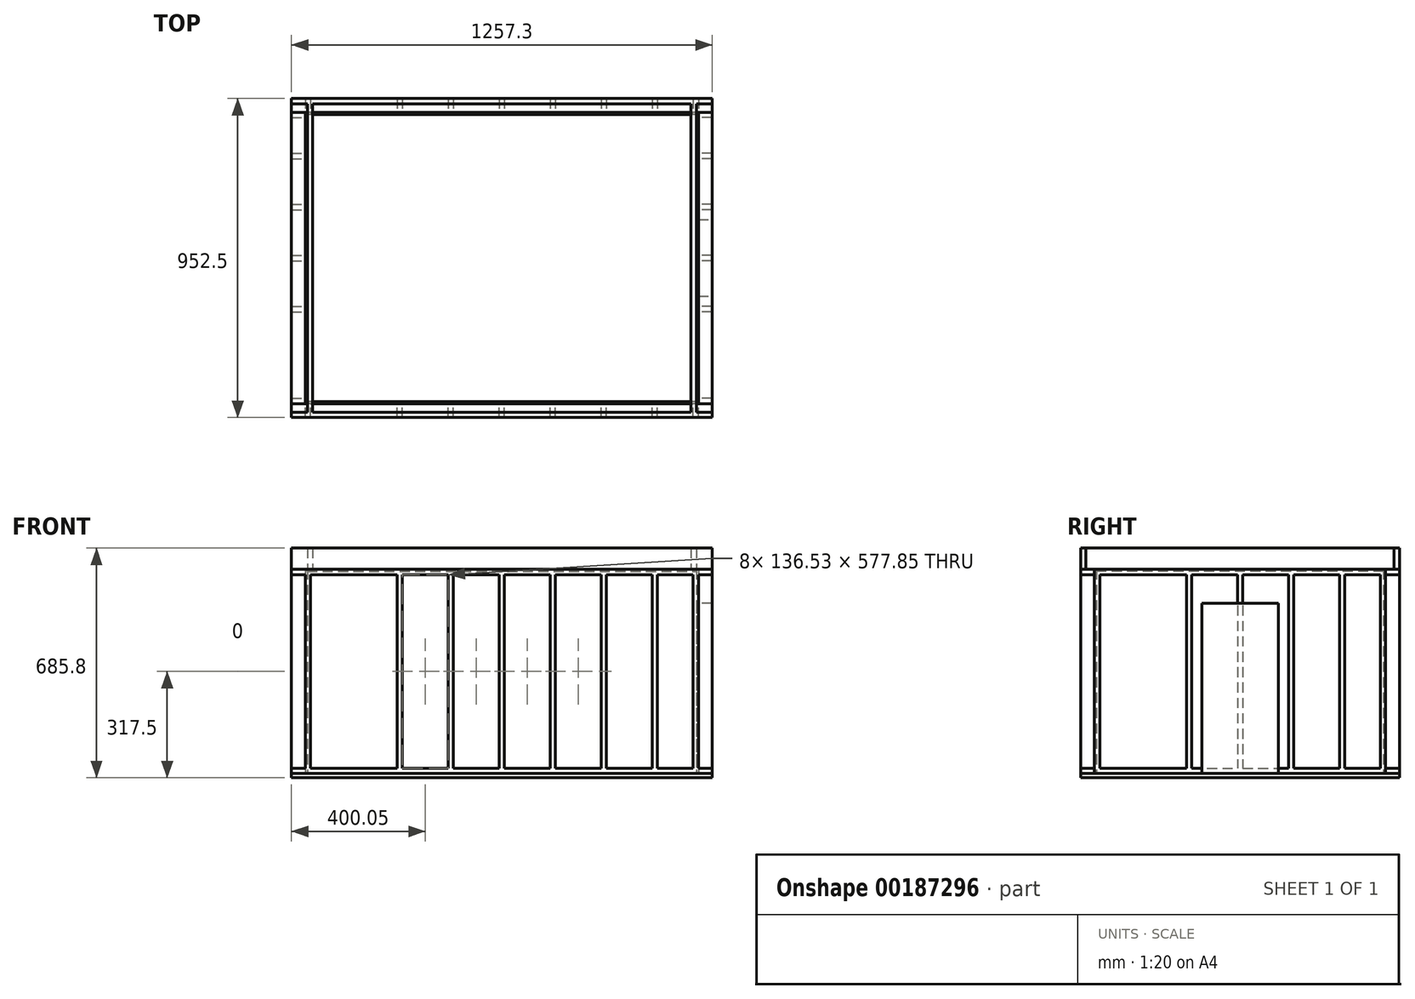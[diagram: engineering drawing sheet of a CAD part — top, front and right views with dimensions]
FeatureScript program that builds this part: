
annotation { "Feature Type Name" : "Feature", "Feature Type Description" : "" }
export const myFeature = defineFeature(function(context is Context, id is Id, definition is map)
    precondition{}
    {
        {
            var Q0;
            Q0=qCreatedBy(makeId("Top.planeOp"),FACE);
            var sketch = newSketch(context, id + "F0", { "sketchPlane" : qUnion([Q0])});
            skLineSegment(sketch, "E0.bottom", {"start": v(587.38, 434.98) * mm, "end": v(-587.38, 434.98) * mm});
            skLineSegment(sketch, "E0.top", {"start": v(587.38, -434.98) * mm, "end": v(-587.38, -434.98) * mm});
            skLineSegment(sketch, "E0.left", {"start": v(587.38, 434.98) * mm, "end": v(587.38, -434.98) * mm});
            skLineSegment(sketch, "E0.right", {"start": v(-587.38, 434.98) * mm, "end": v(-587.38, -434.98) * mm});
            skPoint(sketch, "E0.middle", {"position": v(0, 0) * mm});
            skLineSegment(sketch, "E1.0", {"start": v(581.02, 428.63) * mm, "end": v(-581.03, 428.63) * mm});
            skLineSegment(sketch, "E1.1", {"start": v(581.02, 428.63) * mm, "end": v(581.02, -428.63) * mm});
            skLineSegment(sketch, "E1.2", {"start": v(581.02, -428.63) * mm, "end": v(-581.03, -428.63) * mm});
            skLineSegment(sketch, "E1.3", {"start": v(-581.03, 428.63) * mm, "end": v(-581.03, -428.63) * mm});
            skSolve(sketch);
        }
        {
            var Q0;
            Q0=makeQuery(id+"F0.imprint","IMPRINT",FACE,{"disambiguationData":[TD([[makeQuery(id+"F0.imprint","IMPRINT",EDGE,{"derivedFrom":sQuery(id+"F0.wireOp",EDGE,"E0.bottom")}),1.0]])]});
            extrude(context, id + "F1", {"entities" : qUnion([Q0]), "depth" : 609.6 * mm});
        }
        {
            var Q0;
            Q0=makeQuery(id+"F1.opExtrude","SWEPT_FACE",FACE,{"disambiguationData":[OSD([sQuery(id+"F0.wireOp",EDGE,"E0.top")])]});
            var sketch = newSketch(context, id + "F2", { "sketchPlane" : qUnion([Q0])});
            skLineSegment(sketch, "E2.bottom", {"start": v(-628.65, 0) * mm, "end": v(628.65, 0) * mm});
            skLineSegment(sketch, "E2.top", {"start": v(-628.65, 15.88) * mm, "end": v(628.65, 15.88) * mm});
            skLineSegment(sketch, "E2.left", {"start": v(-628.65, 0) * mm, "end": v(-628.65, 15.88) * mm});
            skLineSegment(sketch, "E2.right", {"start": v(628.65, 0) * mm, "end": v(628.65, 15.88) * mm});
            skLineSegment(sketch, "E3.bottom", {"start": v(628.65, 609.6) * mm, "end": v(-628.65, 609.6) * mm});
            skLineSegment(sketch, "E3.top", {"start": v(628.65, 593.73) * mm, "end": v(-628.65, 593.72) * mm});
            skLineSegment(sketch, "E3.left", {"start": v(628.65, 609.6) * mm, "end": v(628.65, 593.73) * mm});
            skLineSegment(sketch, "E3.right", {"start": v(-628.65, 609.6) * mm, "end": v(-628.65, 593.72) * mm});
            skLineSegment(sketch, "E4.bottom", {"start": v(-587.38, 593.72) * mm, "end": v(-571.5, 593.72) * mm});
            skLineSegment(sketch, "E4.top", {"start": v(-587.38, 15.88) * mm, "end": v(-571.5, 15.88) * mm});
            skLineSegment(sketch, "E4.left", {"start": v(-587.38, 593.72) * mm, "end": v(-587.38, 15.87) * mm});
            skLineSegment(sketch, "E4.right", {"start": v(-571.5, 593.72) * mm, "end": v(-571.5, 15.87) * mm});
            skLineSegment(sketch, "E5.bottom", {"start": v(587.38, 593.72) * mm, "end": v(571.5, 593.72) * mm});
            skLineSegment(sketch, "E5.top", {"start": v(587.38, 15.88) * mm, "end": v(571.5, 15.88) * mm});
            skLineSegment(sketch, "E5.left", {"start": v(587.38, 593.72) * mm, "end": v(587.38, 15.88) * mm});
            skLineSegment(sketch, "E5.right", {"start": v(571.5, 593.72) * mm, "end": v(571.5, 15.88) * mm});
            skLineSegment(sketch, "E6.bottom", {"start": v(-465.14, 593.72) * mm, "end": v(-449.26, 593.72) * mm});
            skLineSegment(sketch, "E6.top", {"start": v(-465.14, 15.87) * mm, "end": v(-449.26, 15.87) * mm});
            skLineSegment(sketch, "E6.left", {"start": v(-465.14, 593.73) * mm, "end": v(-465.14, 15.87) * mm});
            skLineSegment(sketch, "E6.right", {"start": v(-449.26, 593.73) * mm, "end": v(-449.26, 15.87) * mm});
            skLineSegment(sketch, "E7.1.0.0", {"start": v(-296.86, 593.73) * mm, "end": v(-296.86, 15.87) * mm});
            skLineSegment(sketch, "E7.1.0.1", {"start": v(-312.74, 593.73) * mm, "end": v(-312.74, 15.87) * mm});
            skLineSegment(sketch, "E7.1.0.2", {"start": v(-312.74, 593.72) * mm, "end": v(-296.86, 593.72) * mm});
            skLineSegment(sketch, "E7.1.0.3", {"start": v(-312.74, 15.87) * mm, "end": v(-296.86, 15.87) * mm});
            skLineSegment(sketch, "E7.2.0.0", {"start": v(-144.46, 593.73) * mm, "end": v(-144.46, 15.87) * mm});
            skLineSegment(sketch, "E7.2.0.1", {"start": v(-160.34, 593.73) * mm, "end": v(-160.34, 15.87) * mm});
            skLineSegment(sketch, "E7.2.0.2", {"start": v(-160.34, 593.72) * mm, "end": v(-144.46, 593.72) * mm});
            skLineSegment(sketch, "E7.2.0.3", {"start": v(-160.34, 15.87) * mm, "end": v(-144.46, 15.87) * mm});
            skLineSegment(sketch, "E7.3.0.0", {"start": v(7.94, 593.73) * mm, "end": v(7.94, 15.87) * mm});
            skLineSegment(sketch, "E7.3.0.1", {"start": v(-7.94, 593.73) * mm, "end": v(-7.94, 15.87) * mm});
            skLineSegment(sketch, "E7.3.0.2", {"start": v(-7.94, 593.72) * mm, "end": v(7.94, 593.72) * mm});
            skLineSegment(sketch, "E7.3.0.3", {"start": v(-7.94, 15.87) * mm, "end": v(7.94, 15.87) * mm});
            skLineSegment(sketch, "E7.4.0.0", {"start": v(160.34, 593.73) * mm, "end": v(160.34, 15.87) * mm});
            skLineSegment(sketch, "E7.4.0.1", {"start": v(144.46, 593.73) * mm, "end": v(144.46, 15.87) * mm});
            skLineSegment(sketch, "E7.4.0.2", {"start": v(144.46, 593.72) * mm, "end": v(160.34, 593.72) * mm});
            skLineSegment(sketch, "E7.4.0.3", {"start": v(144.46, 15.87) * mm, "end": v(160.34, 15.87) * mm});
            skLineSegment(sketch, "E7.5.0.0", {"start": v(312.74, 593.73) * mm, "end": v(312.74, 15.87) * mm});
            skLineSegment(sketch, "E7.5.0.1", {"start": v(296.86, 593.73) * mm, "end": v(296.86, 15.87) * mm});
            skLineSegment(sketch, "E7.5.0.2", {"start": v(296.86, 593.72) * mm, "end": v(312.74, 593.72) * mm});
            skLineSegment(sketch, "E7.5.0.3", {"start": v(296.86, 15.87) * mm, "end": v(312.74, 15.87) * mm});
            skLineSegment(sketch, "E7.6.0.0", {"start": v(465.14, 593.73) * mm, "end": v(465.14, 15.87) * mm});
            skLineSegment(sketch, "E7.6.0.1", {"start": v(449.26, 593.73) * mm, "end": v(449.26, 15.87) * mm});
            skLineSegment(sketch, "E7.6.0.2", {"start": v(449.26, 593.72) * mm, "end": v(465.14, 593.72) * mm});
            skLineSegment(sketch, "E7.6.0.3", {"start": v(449.26, 15.87) * mm, "end": v(465.14, 15.87) * mm});
            skLineSegment(sketch, "E7.direction1", {"start": v(-449.26, 15.87) * mm, "end": v(-296.86, 15.87) * mm, "construction": true});
            skLineSegment(sketch, "E8", {"start": v(-571.5, 304.8) * mm, "end": v(-465.14, 304.8) * mm, "construction": true});
            skLineSegment(sketch, "E9", {"start": v(465.14, 304.8) * mm, "end": v(571.5, 304.8) * mm, "construction": true});
            skSolve(sketch);
        }
        {
            var Q0;
            Q0 = qSketchRegion(id + "F2", true);
            var Q1;
            Q1=makeQuery(id+"F2.imprint","IMPRINT",FACE,{"disambiguationData":[TD([[makeQuery(id+"F2.imprint","IMPRINT",EDGE,{"derivedFrom":sQuery(id+"F2.wireOp",EDGE,"E6.bottom")}),-1.0]])]});
            var Q2;
            Q2=makeQuery(id+"F2.imprint","IMPRINT",FACE,{"disambiguationData":[TD([[makeQuery(id+"F2.imprint","IMPRINT",EDGE,{"derivedFrom":sQuery(id+"F2.wireOp",EDGE,"E7.1.0.0")}),-1.0]])]});
            var Q3;
            Q3=makeQuery(id+"F2.imprint","IMPRINT",FACE,{"disambiguationData":[TD([[makeQuery(id+"F2.imprint","IMPRINT",EDGE,{"derivedFrom":sQuery(id+"F2.wireOp",EDGE,"E7.2.0.0")}),-1.0]])]});
            var Q4;
            Q4=makeQuery(id+"F2.imprint","IMPRINT",FACE,{"disambiguationData":[TD([[makeQuery(id+"F2.imprint","IMPRINT",EDGE,{"derivedFrom":sQuery(id+"F2.wireOp",EDGE,"E7.3.0.0")}),-1.0]])]});
            var Q5;
            Q5=makeQuery(id+"F2.imprint","IMPRINT",FACE,{"disambiguationData":[TD([[makeQuery(id+"F2.imprint","IMPRINT",EDGE,{"derivedFrom":sQuery(id+"F2.wireOp",EDGE,"E7.4.0.0")}),-1.0]])]});
            var Q6;
            Q6=makeQuery(id+"F2.imprint","IMPRINT",FACE,{"disambiguationData":[TD([[makeQuery(id+"F2.imprint","IMPRINT",EDGE,{"derivedFrom":sQuery(id+"F2.wireOp",EDGE,"E7.5.0.0")}),-1.0]])]});
            var Q7;
            Q7=makeQuery(id+"F2.imprint","IMPRINT",FACE,{"disambiguationData":[TD([[makeQuery(id+"F2.imprint","IMPRINT",EDGE,{"derivedFrom":sQuery(id+"F2.wireOp",EDGE,"E7.6.0.0")}),-1.0]])]});
            extrude(context, id + "F3", {"entities" : qUnion([Q0, Q1, Q2, Q3, Q4, Q5, Q6, Q7]), "depth" : 41.27 * mm});
        }
        {
            var Q0;
            Q0=makeQuery(id+"F3.opExtrude","SWEPT_BODY",BODY,{"disambiguationData":[OSD([sQuery(id+"F2.wireOp",EDGE,"E2.bottom"),sQuery(id+"F2.wireOp",EDGE,"E2.top"),sQuery(id+"F2.wireOp",EDGE,"E2.left"),sQuery(id+"F2.wireOp",EDGE,"E2.right"),sQuery(id+"F2.wireOp",EDGE,"E3.bottom"),sQuery(id+"F2.wireOp",EDGE,"E3.top"),sQuery(id+"F2.wireOp",EDGE,"E3.left"),sQuery(id+"F2.wireOp",EDGE,"E3.right"),sQuery(id+"F2.wireOp",EDGE,"E4.left"),sQuery(id+"F2.wireOp",EDGE,"E4.right"),sQuery(id+"F2.wireOp",EDGE,"E5.left"),sQuery(id+"F2.wireOp",EDGE,"E5.right"),sQuery(id+"F2.wireOp",EDGE,"E6.left"),sQuery(id+"F2.wireOp",EDGE,"E6.right"),sQuery(id+"F2.wireOp",EDGE,"E7.1.0.0"),sQuery(id+"F2.wireOp",EDGE,"E7.1.0.1"),sQuery(id+"F2.wireOp",EDGE,"E7.2.0.0"),sQuery(id+"F2.wireOp",EDGE,"E7.2.0.1"),sQuery(id+"F2.wireOp",EDGE,"E7.3.0.0"),sQuery(id+"F2.wireOp",EDGE,"E7.3.0.1"),sQuery(id+"F2.wireOp",EDGE,"E7.4.0.0"),sQuery(id+"F2.wireOp",EDGE,"E7.4.0.1"),sQuery(id+"F2.wireOp",EDGE,"E7.5.0.0"),sQuery(id+"F2.wireOp",EDGE,"E7.5.0.1"),sQuery(id+"F2.wireOp",EDGE,"E7.6.0.0"),sQuery(id+"F2.wireOp",EDGE,"E7.6.0.1")])]});
            var Q1;
            Q1=qCreatedBy(makeId("Front.planeOp"),FACE);
            mirror(context, id + "F4", {"entities" : qUnion([Q0]), "mirrorPlane" : qUnion([Q1])});
        }
        {
            var Q0;
            Q0=makeQuery(id+"F1.opExtrude","SWEPT_FACE",FACE,{"disambiguationData":[OSD([sQuery(id+"F0.wireOp",EDGE,"E0.left")])]});
            var sketch = newSketch(context, id + "F5", { "sketchPlane" : qUnion([Q0])});
            skLineSegment(sketch, "E10.bottom", {"start": v(-434.98, 0) * mm, "end": v(434.98, 0) * mm});
            skLineSegment(sketch, "E10.top", {"start": v(-434.98, 15.88) * mm, "end": v(434.98, 15.88) * mm});
            skLineSegment(sketch, "E10.left", {"start": v(-434.98, 0) * mm, "end": v(-434.98, 15.88) * mm});
            skLineSegment(sketch, "E10.right", {"start": v(434.98, 0) * mm, "end": v(434.98, 15.88) * mm});
            skLineSegment(sketch, "E11.bottom", {"start": v(-434.98, 609.6) * mm, "end": v(434.98, 609.6) * mm});
            skLineSegment(sketch, "E11.top", {"start": v(-434.98, 593.73) * mm, "end": v(434.98, 593.73) * mm});
            skLineSegment(sketch, "E11.left", {"start": v(-434.98, 609.6) * mm, "end": v(-434.98, 593.73) * mm});
            skLineSegment(sketch, "E11.right", {"start": v(434.98, 609.6) * mm, "end": v(434.98, 593.73) * mm});
            skLineSegment(sketch, "E12.bottom", {"start": v(-434.98, 593.73) * mm, "end": v(-419.1, 593.73) * mm});
            skLineSegment(sketch, "E12.top", {"start": v(-434.98, 15.88) * mm, "end": v(-419.1, 15.88) * mm});
            skLineSegment(sketch, "E12.left", {"start": v(-434.98, 593.73) * mm, "end": v(-434.98, 15.88) * mm});
            skLineSegment(sketch, "E12.right", {"start": v(-419.1, 593.73) * mm, "end": v(-419.1, 15.88) * mm});
            skLineSegment(sketch, "E13.bottom", {"start": v(434.98, 593.73) * mm, "end": v(419.1, 593.73) * mm});
            skLineSegment(sketch, "E13.top", {"start": v(434.98, 15.88) * mm, "end": v(419.1, 15.88) * mm});
            skLineSegment(sketch, "E13.left", {"start": v(434.98, 593.73) * mm, "end": v(434.98, 15.88) * mm});
            skLineSegment(sketch, "E13.right", {"start": v(419.1, 593.73) * mm, "end": v(419.1, 15.87) * mm});
            skLineSegment(sketch, "E14.bottom", {"start": v(-312.74, 593.73) * mm, "end": v(-296.86, 593.73) * mm});
            skLineSegment(sketch, "E14.top", {"start": v(-312.74, 15.88) * mm, "end": v(-296.86, 15.88) * mm});
            skLineSegment(sketch, "E14.left", {"start": v(-312.74, 593.73) * mm, "end": v(-312.74, 15.87) * mm});
            skLineSegment(sketch, "E14.right", {"start": v(-296.86, 593.73) * mm, "end": v(-296.86, 15.87) * mm});
            skLineSegment(sketch, "E15.1.0.0", {"start": v(-144.46, 593.73) * mm, "end": v(-144.46, 15.87) * mm});
            skLineSegment(sketch, "E15.1.0.1", {"start": v(-160.34, 593.73) * mm, "end": v(-160.34, 15.87) * mm});
            skLineSegment(sketch, "E15.1.0.2", {"start": v(-160.34, 15.88) * mm, "end": v(-144.46, 15.88) * mm});
            skLineSegment(sketch, "E15.1.0.3", {"start": v(-160.34, 593.73) * mm, "end": v(-144.46, 593.73) * mm});
            skLineSegment(sketch, "E15.2.0.0", {"start": v(7.94, 593.73) * mm, "end": v(7.94, 15.87) * mm});
            skLineSegment(sketch, "E15.2.0.1", {"start": v(-7.94, 593.73) * mm, "end": v(-7.94, 15.87) * mm});
            skLineSegment(sketch, "E15.2.0.2", {"start": v(-7.94, 15.88) * mm, "end": v(7.94, 15.88) * mm});
            skLineSegment(sketch, "E15.2.0.3", {"start": v(-7.94, 593.73) * mm, "end": v(7.94, 593.73) * mm});
            skLineSegment(sketch, "E15.3.0.0", {"start": v(160.34, 593.73) * mm, "end": v(160.34, 15.87) * mm});
            skLineSegment(sketch, "E15.3.0.1", {"start": v(144.46, 593.73) * mm, "end": v(144.46, 15.87) * mm});
            skLineSegment(sketch, "E15.3.0.2", {"start": v(144.46, 15.88) * mm, "end": v(160.34, 15.88) * mm});
            skLineSegment(sketch, "E15.3.0.3", {"start": v(144.46, 593.73) * mm, "end": v(160.34, 593.73) * mm});
            skLineSegment(sketch, "E15.4.0.0", {"start": v(312.74, 593.73) * mm, "end": v(312.74, 15.87) * mm});
            skLineSegment(sketch, "E15.4.0.1", {"start": v(296.86, 593.73) * mm, "end": v(296.86, 15.87) * mm});
            skLineSegment(sketch, "E15.4.0.2", {"start": v(296.86, 15.88) * mm, "end": v(312.74, 15.88) * mm});
            skLineSegment(sketch, "E15.4.0.3", {"start": v(296.86, 593.73) * mm, "end": v(312.74, 593.73) * mm});
            skLineSegment(sketch, "E15.direction1", {"start": v(-296.86, 15.87) * mm, "end": v(-144.46, 15.87) * mm, "construction": true});
            skLineSegment(sketch, "E16", {"start": v(-419.1, 304.8) * mm, "end": v(-312.74, 304.8) * mm, "construction": true});
            skLineSegment(sketch, "E17", {"start": v(312.74, 304.8) * mm, "end": v(419.1, 304.8) * mm, "construction": true});
            skSolve(sketch);
        }
        {
            var Q0;
            Q0 = qSketchRegion(id + "F5", true);
            var Q1;
            Q1=makeQuery(id+"F5.imprint","IMPRINT",FACE,{"disambiguationData":[TD([[makeQuery(id+"F5.imprint","IMPRINT",EDGE,{"derivedFrom":sQuery(id+"F5.wireOp",EDGE,"E14.bottom")}),-1.0]])]});
            var Q2;
            Q2=makeQuery(id+"F5.imprint","IMPRINT",FACE,{"disambiguationData":[TD([[makeQuery(id+"F5.imprint","IMPRINT",EDGE,{"derivedFrom":sQuery(id+"F5.wireOp",EDGE,"E15.1.0.0")}),-1.0]])]});
            var Q3;
            Q3=makeQuery(id+"F5.imprint","IMPRINT",FACE,{"disambiguationData":[TD([[makeQuery(id+"F5.imprint","IMPRINT",EDGE,{"derivedFrom":sQuery(id+"F5.wireOp",EDGE,"E15.2.0.0")}),-1.0]])]});
            var Q4;
            Q4=makeQuery(id+"F5.imprint","IMPRINT",FACE,{"disambiguationData":[TD([[makeQuery(id+"F5.imprint","IMPRINT",EDGE,{"derivedFrom":sQuery(id+"F5.wireOp",EDGE,"E15.3.0.0")}),-1.0]])]});
            var Q5;
            Q5=makeQuery(id+"F5.imprint","IMPRINT",FACE,{"disambiguationData":[TD([[makeQuery(id+"F5.imprint","IMPRINT",EDGE,{"derivedFrom":sQuery(id+"F5.wireOp",EDGE,"E15.4.0.0")}),-1.0]])]});
            extrude(context, id + "F6", {"entities" : qUnion([Q0, Q1, Q2, Q3, Q4, Q5]), "depth" : 41.27 * mm});
        }
        {
            var Q0;
            Q0=makeQuery(id+"F6.opExtrude","SWEPT_BODY",BODY,{"disambiguationData":[OSD([sQuery(id+"F5.wireOp",EDGE,"E10.bottom"),sQuery(id+"F5.wireOp",EDGE,"E10.top"),sQuery(id+"F5.wireOp",EDGE,"E10.left"),sQuery(id+"F5.wireOp",EDGE,"E10.right"),sQuery(id+"F5.wireOp",EDGE,"E11.bottom"),sQuery(id+"F5.wireOp",EDGE,"E11.top"),sQuery(id+"F5.wireOp",EDGE,"E11.left"),sQuery(id+"F5.wireOp",EDGE,"E11.right"),sQuery(id+"F5.wireOp",EDGE,"E12.left"),sQuery(id+"F5.wireOp",EDGE,"E12.right"),sQuery(id+"F5.wireOp",EDGE,"E13.left"),sQuery(id+"F5.wireOp",EDGE,"E13.right"),sQuery(id+"F5.wireOp",EDGE,"E14.left"),sQuery(id+"F5.wireOp",EDGE,"E14.right"),sQuery(id+"F5.wireOp",EDGE,"E15.1.0.0"),sQuery(id+"F5.wireOp",EDGE,"E15.1.0.1"),sQuery(id+"F5.wireOp",EDGE,"E15.2.0.0"),sQuery(id+"F5.wireOp",EDGE,"E15.2.0.1"),sQuery(id+"F5.wireOp",EDGE,"E15.3.0.0"),sQuery(id+"F5.wireOp",EDGE,"E15.3.0.1"),sQuery(id+"F5.wireOp",EDGE,"E15.4.0.0"),sQuery(id+"F5.wireOp",EDGE,"E15.4.0.1")])]});
            var Q1;
            Q1=qCreatedBy(makeId("Right.planeOp"),FACE);
            mirror(context, id + "F7", {"entities" : qUnion([Q0]), "mirrorPlane" : qUnion([Q1])});
        }
        {
            var Q0;
            Q0=makeQuery(id+"F3.opExtrude","SWEPT_FACE",FACE,{"disambiguationData":[OSD([sQuery(id+"F2.wireOp",EDGE,"E3.bottom")])]});
            var sketch = newSketch(context, id + "F8", { "sketchPlane" : qUnion([Q0])});
            skLineSegment(sketch, "E18.bottom", {"start": v(-581.03, 428.63) * mm, "end": v(581.02, 428.63) * mm});
            skLineSegment(sketch, "E18.top", {"start": v(-581.03, -428.63) * mm, "end": v(581.02, -428.63) * mm});
            skLineSegment(sketch, "E18.left", {"start": v(-581.03, 428.63) * mm, "end": v(-581.03, -428.63) * mm});
            skLineSegment(sketch, "E18.right", {"start": v(581.02, 428.63) * mm, "end": v(581.02, -428.63) * mm});
            skSolve(sketch);
        }
        {
            var Q0;
            Q0=makeQuery(id+"F8.imprint","IMPRINT",FACE,{"disambiguationData":[TD([[makeQuery(id+"F8.imprint","IMPRINT",EDGE,{"derivedFrom":sQuery(id+"F8.wireOp",EDGE,"E18.bottom")}),-1.0]])]});
            extrude(context, id + "F9", {"entities" : qUnion([Q0]), "oppositeDirection" : true, "depth" : 6.35 * mm});
        }
        {
            var Q0;
            Q0=makeQuery(id+"F3.opExtrude","SWEPT_FACE",FACE,{"disambiguationData":[OSD([sQuery(id+"F2.wireOp",EDGE,"E3.bottom")])]});
            var sketch = newSketch(context, id + "F10", { "sketchPlane" : qUnion([Q0])});
            skLineSegment(sketch, "E19.bottom", {"start": v(-628.65, -476.25) * mm, "end": v(628.65, -476.25) * mm});
            skLineSegment(sketch, "E19.top", {"start": v(-628.65, -460.38) * mm, "end": v(628.65, -460.38) * mm});
            skLineSegment(sketch, "E19.left", {"start": v(-628.65, -476.25) * mm, "end": v(-628.65, -460.38) * mm});
            skLineSegment(sketch, "E19.right", {"start": v(628.65, -476.25) * mm, "end": v(628.65, -460.38) * mm});
            skLineSegment(sketch, "E20.bottom", {"start": v(628.65, 476.25) * mm, "end": v(-628.65, 476.25) * mm});
            skLineSegment(sketch, "E20.top", {"start": v(628.65, 460.38) * mm, "end": v(-628.65, 460.38) * mm});
            skLineSegment(sketch, "E20.left", {"start": v(628.65, 476.25) * mm, "end": v(628.65, 460.38) * mm});
            skLineSegment(sketch, "E20.right", {"start": v(-628.65, 476.25) * mm, "end": v(-628.65, 460.38) * mm});
            skLineSegment(sketch, "E21.bottom", {"start": v(-581.03, 460.38) * mm, "end": v(-565.15, 460.38) * mm});
            skLineSegment(sketch, "E21.top", {"start": v(-581.03, -460.38) * mm, "end": v(-565.15, -460.38) * mm});
            skLineSegment(sketch, "E21.left", {"start": v(-581.03, 460.38) * mm, "end": v(-581.03, -460.38) * mm});
            skLineSegment(sketch, "E21.right", {"start": v(-565.15, 460.38) * mm, "end": v(-565.15, -460.38) * mm});
            skLineSegment(sketch, "E22.bottom", {"start": v(581.02, 460.38) * mm, "end": v(565.15, 460.38) * mm});
            skLineSegment(sketch, "E22.top", {"start": v(581.02, -460.38) * mm, "end": v(565.15, -460.38) * mm});
            skLineSegment(sketch, "E22.left", {"start": v(581.02, 460.38) * mm, "end": v(581.02, -460.38) * mm});
            skLineSegment(sketch, "E22.right", {"start": v(565.15, 460.38) * mm, "end": v(565.15, -460.38) * mm});
            skLineSegment(sketch, "E23.bottom", {"start": v(-465.14, 460.38) * mm, "end": v(-449.26, 460.38) * mm});
            skLineSegment(sketch, "E23.top", {"start": v(-465.14, -460.38) * mm, "end": v(-449.26, -460.38) * mm});
            skLineSegment(sketch, "E23.left", {"start": v(-465.14, 460.38) * mm, "end": v(-465.14, -460.38) * mm});
            skLineSegment(sketch, "E23.right", {"start": v(-449.26, 460.38) * mm, "end": v(-449.26, -460.38) * mm});
            skLineSegment(sketch, "E24.1.0.0", {"start": v(-296.86, 460.38) * mm, "end": v(-296.86, -460.38) * mm});
            skLineSegment(sketch, "E24.1.0.1", {"start": v(-312.74, 460.38) * mm, "end": v(-312.74, -460.38) * mm});
            skLineSegment(sketch, "E24.1.0.2", {"start": v(-312.74, -460.38) * mm, "end": v(-296.86, -460.38) * mm});
            skLineSegment(sketch, "E24.1.0.3", {"start": v(-312.74, 460.38) * mm, "end": v(-296.86, 460.38) * mm});
            skLineSegment(sketch, "E24.2.0.0", {"start": v(-144.46, 460.38) * mm, "end": v(-144.46, -460.38) * mm});
            skLineSegment(sketch, "E24.2.0.1", {"start": v(-160.34, 460.38) * mm, "end": v(-160.34, -460.38) * mm});
            skLineSegment(sketch, "E24.2.0.2", {"start": v(-160.34, -460.38) * mm, "end": v(-144.46, -460.38) * mm});
            skLineSegment(sketch, "E24.2.0.3", {"start": v(-160.34, 460.38) * mm, "end": v(-144.46, 460.38) * mm});
            skLineSegment(sketch, "E24.3.0.0", {"start": v(7.94, 460.38) * mm, "end": v(7.94, -460.38) * mm});
            skLineSegment(sketch, "E24.3.0.1", {"start": v(-7.94, 460.38) * mm, "end": v(-7.94, -460.38) * mm});
            skLineSegment(sketch, "E24.3.0.2", {"start": v(-7.94, -460.38) * mm, "end": v(7.94, -460.38) * mm});
            skLineSegment(sketch, "E24.3.0.3", {"start": v(-7.94, 460.38) * mm, "end": v(7.94, 460.38) * mm});
            skLineSegment(sketch, "E24.4.0.0", {"start": v(160.34, 460.38) * mm, "end": v(160.34, -460.38) * mm});
            skLineSegment(sketch, "E24.4.0.1", {"start": v(144.46, 460.38) * mm, "end": v(144.46, -460.38) * mm});
            skLineSegment(sketch, "E24.4.0.2", {"start": v(144.46, -460.38) * mm, "end": v(160.34, -460.38) * mm});
            skLineSegment(sketch, "E24.4.0.3", {"start": v(144.46, 460.38) * mm, "end": v(160.34, 460.38) * mm});
            skLineSegment(sketch, "E24.5.0.0", {"start": v(312.74, 460.38) * mm, "end": v(312.74, -460.38) * mm});
            skLineSegment(sketch, "E24.5.0.1", {"start": v(296.86, 460.38) * mm, "end": v(296.86, -460.38) * mm});
            skLineSegment(sketch, "E24.5.0.2", {"start": v(296.86, -460.38) * mm, "end": v(312.74, -460.38) * mm});
            skLineSegment(sketch, "E24.5.0.3", {"start": v(296.86, 460.38) * mm, "end": v(312.74, 460.38) * mm});
            skLineSegment(sketch, "E24.6.0.0", {"start": v(465.14, 460.38) * mm, "end": v(465.14, -460.38) * mm});
            skLineSegment(sketch, "E24.6.0.1", {"start": v(449.26, 460.38) * mm, "end": v(449.26, -460.38) * mm});
            skLineSegment(sketch, "E24.6.0.2", {"start": v(449.26, -460.38) * mm, "end": v(465.14, -460.38) * mm});
            skLineSegment(sketch, "E24.6.0.3", {"start": v(449.26, 460.38) * mm, "end": v(465.14, 460.38) * mm});
            skLineSegment(sketch, "E24.direction1", {"start": v(-449.26, -460.38) * mm, "end": v(-296.86, -460.38) * mm, "construction": true});
            skLineSegment(sketch, "E25", {"start": v(-565.15, 0) * mm, "end": v(-465.14, 0) * mm, "construction": true});
            skLineSegment(sketch, "E26", {"start": v(465.14, 0) * mm, "end": v(565.15, 0) * mm, "construction": true});
            skSolve(sketch);
        }
        {
            var Q0;
            Q0 = qSketchRegion(id + "F10", true);
            var Q1;
            {var subQ0=sQuery(id+"F10.wireOp",EDGE,"E23.bottom");Q1=makeQuery(id+"F10.imprint","IMPRINT",FACE,{"disambiguationData":[TD([[makeQuery(id+"F10.imprint","IMPRINT",EDGE,{"derivedFrom":subQ0}),-1.0]])]});}
            var Q2;
            {var subQ0=sQuery(id+"F10.wireOp",EDGE,"E24.1.0.3");Q2=makeQuery(id+"F10.imprint","IMPRINT",FACE,{"disambiguationData":[TD([[makeQuery(id+"F10.imprint","IMPRINT",EDGE,{"derivedFrom":subQ0}),-1.0]])]});}
            var Q3;
            {var subQ0=sQuery(id+"F10.wireOp",EDGE,"E24.2.0.3");Q3=makeQuery(id+"F10.imprint","IMPRINT",FACE,{"disambiguationData":[TD([[makeQuery(id+"F10.imprint","IMPRINT",EDGE,{"derivedFrom":subQ0}),-1.0]])]});}
            var Q4;
            {var subQ0=sQuery(id+"F10.wireOp",EDGE,"E24.3.0.3");Q4=makeQuery(id+"F10.imprint","IMPRINT",FACE,{"disambiguationData":[TD([[makeQuery(id+"F10.imprint","IMPRINT",EDGE,{"derivedFrom":subQ0}),-1.0]])]});}
            var Q5;
            {var subQ0=sQuery(id+"F10.wireOp",EDGE,"E24.4.0.3");Q5=makeQuery(id+"F10.imprint","IMPRINT",FACE,{"disambiguationData":[TD([[makeQuery(id+"F10.imprint","IMPRINT",EDGE,{"derivedFrom":subQ0}),-1.0]])]});}
            var Q6;
            {var subQ0=sQuery(id+"F10.wireOp",EDGE,"E24.5.0.3");Q6=makeQuery(id+"F10.imprint","IMPRINT",FACE,{"disambiguationData":[TD([[makeQuery(id+"F10.imprint","IMPRINT",EDGE,{"derivedFrom":subQ0}),-1.0]])]});}
            var Q7;
            {var subQ0=sQuery(id+"F10.wireOp",EDGE,"E24.6.0.3");Q7=makeQuery(id+"F10.imprint","IMPRINT",FACE,{"disambiguationData":[TD([[makeQuery(id+"F10.imprint","IMPRINT",EDGE,{"derivedFrom":subQ0}),-1.0]])]});}
            var Q8;
            {var subQ0=sQuery(id+"F10.wireOp",EDGE,"E23.top");Q8=makeQuery(id+"F10.imprint","IMPRINT",FACE,{"disambiguationData":[TD([[makeQuery(id+"F10.imprint","IMPRINT",EDGE,{"derivedFrom":subQ0}),1.0]])]});}
            var Q9;
            {var subQ0=sQuery(id+"F10.wireOp",EDGE,"E24.1.0.2");Q9=makeQuery(id+"F10.imprint","IMPRINT",FACE,{"disambiguationData":[TD([[makeQuery(id+"F10.imprint","IMPRINT",EDGE,{"derivedFrom":subQ0}),1.0]])]});}
            var Q10;
            {var subQ0=sQuery(id+"F10.wireOp",EDGE,"E24.2.0.2");Q10=makeQuery(id+"F10.imprint","IMPRINT",FACE,{"disambiguationData":[TD([[makeQuery(id+"F10.imprint","IMPRINT",EDGE,{"derivedFrom":subQ0}),1.0]])]});}
            var Q11;
            {var subQ0=sQuery(id+"F10.wireOp",EDGE,"E24.3.0.2");Q11=makeQuery(id+"F10.imprint","IMPRINT",FACE,{"disambiguationData":[TD([[makeQuery(id+"F10.imprint","IMPRINT",EDGE,{"derivedFrom":subQ0}),1.0]])]});}
            var Q12;
            {var subQ0=sQuery(id+"F10.wireOp",EDGE,"E24.4.0.2");Q12=makeQuery(id+"F10.imprint","IMPRINT",FACE,{"disambiguationData":[TD([[makeQuery(id+"F10.imprint","IMPRINT",EDGE,{"derivedFrom":subQ0}),1.0]])]});}
            var Q13;
            {var subQ0=sQuery(id+"F10.wireOp",EDGE,"E24.5.0.2");Q13=makeQuery(id+"F10.imprint","IMPRINT",FACE,{"disambiguationData":[TD([[makeQuery(id+"F10.imprint","IMPRINT",EDGE,{"derivedFrom":subQ0}),1.0]])]});}
            var Q14;
            {var subQ0=sQuery(id+"F10.wireOp",EDGE,"E24.6.0.2");Q14=makeQuery(id+"F10.imprint","IMPRINT",FACE,{"disambiguationData":[TD([[makeQuery(id+"F10.imprint","IMPRINT",EDGE,{"derivedFrom":subQ0}),1.0]])]});}
            extrude(context, id + "F11", {"entities" : qUnion([Q0, Q1, Q2, Q3, Q4, Q5, Q6, Q7, Q8, Q9, Q10, Q11, Q12, Q13, Q14]), "depth" : 63.5 * mm});
        }
        {
            var Q0;
            Q0=makeQuery(id+"F6.opExtrude","CAP_FACE",FACE,{"disambiguationData":[OSD([sQuery(id+"F5.wireOp",EDGE,"E10.bottom"),sQuery(id+"F5.wireOp",EDGE,"E10.top"),sQuery(id+"F5.wireOp",EDGE,"E10.left"),sQuery(id+"F5.wireOp",EDGE,"E10.right"),sQuery(id+"F5.wireOp",EDGE,"E11.bottom"),sQuery(id+"F5.wireOp",EDGE,"E11.top"),sQuery(id+"F5.wireOp",EDGE,"E11.left"),sQuery(id+"F5.wireOp",EDGE,"E11.right"),sQuery(id+"F5.wireOp",EDGE,"E12.left"),sQuery(id+"F5.wireOp",EDGE,"E12.right"),sQuery(id+"F5.wireOp",EDGE,"E13.left"),sQuery(id+"F5.wireOp",EDGE,"E13.right"),sQuery(id+"F5.wireOp",EDGE,"E14.left"),sQuery(id+"F5.wireOp",EDGE,"E14.right"),sQuery(id+"F5.wireOp",EDGE,"E15.1.0.0"),sQuery(id+"F5.wireOp",EDGE,"E15.1.0.1"),sQuery(id+"F5.wireOp",EDGE,"E15.2.0.0"),sQuery(id+"F5.wireOp",EDGE,"E15.2.0.1"),sQuery(id+"F5.wireOp",EDGE,"E15.3.0.0"),sQuery(id+"F5.wireOp",EDGE,"E15.3.0.1"),sQuery(id+"F5.wireOp",EDGE,"E15.4.0.0"),sQuery(id+"F5.wireOp",EDGE,"E15.4.0.1")])],"isStart":false});
            var sketch = newSketch(context, id + "F12", { "sketchPlane" : qUnion([Q0])});
            skLineSegment(sketch, "E27.bottom", {"start": v(-114.3, 508) * mm, "end": v(114.3, 508) * mm});
            skLineSegment(sketch, "E27.top", {"start": v(-114.3, 0) * mm, "end": v(114.3, 0) * mm});
            skLineSegment(sketch, "E27.left", {"start": v(-114.3, 508) * mm, "end": v(-114.3, 0) * mm});
            skLineSegment(sketch, "E27.right", {"start": v(114.3, 508) * mm, "end": v(114.3, 0) * mm});
            skLineSegment(sketch, "E28", {"start": v(-144.46, 304.8) * mm, "end": v(-114.3, 304.8) * mm, "construction": true});
            skLineSegment(sketch, "E29", {"start": v(144.46, 304.8) * mm, "end": v(114.3, 304.8) * mm, "construction": true});
            skSolve(sketch);
        }
        {
            var Q0;
            {var subQ0=sQuery(id+"F12.wireOp",EDGE,"E27.left");var subQ1=sQuery(id+"F12.wireOp",EDGE,"E27.bottom");var subQ2=makeQuery(id+"F12.imprint","INTERSECT",VERTEX,{"derivedFrom":[subQ1,subQ0]});Q0=makeQuery(id+"F12.imprint","IMPRINT",FACE,{"disambiguationData":[TD([[makeQuery(id+"F12.imprint","IMPRINT",EDGE,{"disambiguationData":[TD([[subQ2,-1.0]])],"derivedFrom":subQ1}),-1.0]])]});}
            var Q1;
            {var subQ0=sQuery(id+"F12.wireOp",EDGE,"E27.right");var subQ1=sQuery(id+"F12.wireOp",EDGE,"E27.bottom");var subQ2=makeQuery(id+"F12.imprint","INTERSECT",VERTEX,{"derivedFrom":[subQ1,subQ0]});Q1=makeQuery(id+"F12.imprint","IMPRINT",FACE,{"disambiguationData":[TD([[makeQuery(id+"F12.imprint","IMPRINT",EDGE,{"disambiguationData":[TD([[subQ2,1.0]])],"derivedFrom":subQ1}),-1.0]])]});}
            var Q2;
            {var subQ1=sQuery(id+"F12.wireOp",EDGE,"E27.top");Q2=makeQuery(id+"F12.imprint","IMPRINT",FACE,{"disambiguationData":[TD([[makeQuery(id+"F12.imprint","IMPRINT",EDGE,{"derivedFrom":subQ1}),-1.0]])]});}
            extrude(context, id + "F13", {"entities" : qUnion([Q0, Q1, Q2]), "operationType" : NewBodyOperationType.REMOVE, "oppositeDirection" : true, "depth" : 76.2 * mm});
        }
        {
            var Q0;
            Q0=makeQuery(id+"F3.opExtrude","SWEPT_FACE",FACE,{"disambiguationData":[OSD([sQuery(id+"F2.wireOp",EDGE,"E2.bottom")])]});
            var sketch = newSketch(context, id + "F14", { "sketchPlane" : qUnion([Q0])});
            skLineSegment(sketch, "E30.bottom", {"start": v(-628.65, 476.25) * mm, "end": v(628.65, 476.25) * mm});
            skLineSegment(sketch, "E30.top", {"start": v(-628.65, -476.25) * mm, "end": v(628.65, -476.25) * mm});
            skLineSegment(sketch, "E30.left", {"start": v(-628.65, 476.25) * mm, "end": v(-628.65, -476.25) * mm});
            skLineSegment(sketch, "E30.right", {"start": v(628.65, 476.25) * mm, "end": v(628.65, -476.25) * mm});
            skSolve(sketch);
        }
        {
            var Q0;
            {var subQ0=sQuery(id+"F14.wireOp",EDGE,"E30.top");Q0=makeQuery(id+"F14.imprint","IMPRINT",FACE,{"disambiguationData":[TD([[makeQuery(id+"F14.imprint","IMPRINT",EDGE,{"derivedFrom":subQ0}),1.0]])]});}
            var Q1;
            {var subQ0=sQuery(id+"F14.wireOp",EDGE,"E30.bottom");Q1=makeQuery(id+"F14.imprint","IMPRINT",FACE,{"disambiguationData":[TD([[makeQuery(id+"F14.imprint","IMPRINT",EDGE,{"derivedFrom":subQ0}),-1.0]])]});}
            extrude(context, id + "F15", {"entities" : qUnion([Q0, Q1]), "depth" : 12.7 * mm});
        }
    });
